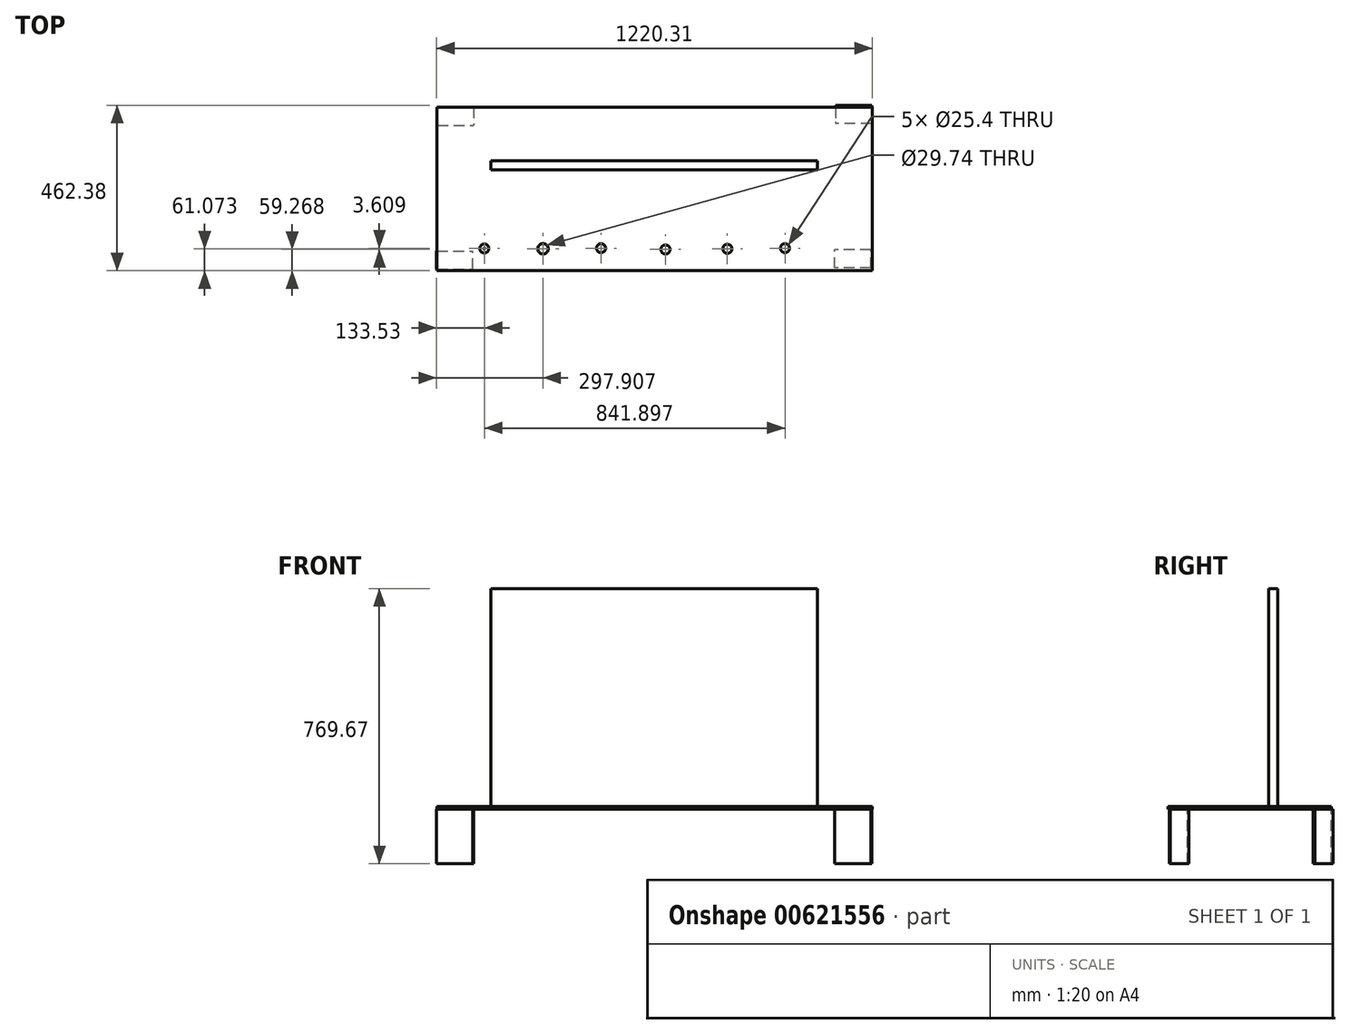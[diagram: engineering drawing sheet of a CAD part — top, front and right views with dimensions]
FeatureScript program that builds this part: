
annotation { "Feature Type Name" : "Feature", "Feature Type Description" : "" }
export const myFeature = defineFeature(function(context is Context, id is Id, definition is map)
    precondition{}
    {
        {
            var Q0;
            Q0=qCreatedBy(makeId("Front.planeOp"),FACE);
            var sketch = newSketch(context, id + "F0", { "sketchPlane" : qUnion([Q0])});
            skLineSegment(sketch, "E0.bottom", {"start": v(-46.83, 617.27) * mm, "end": v(867.57, 617.27) * mm});
            skLineSegment(sketch, "E0.top", {"start": v(-46.83, 7.67) * mm, "end": v(867.57, 7.67) * mm});
            skLineSegment(sketch, "E0.left", {"start": v(-46.83, 617.27) * mm, "end": v(-46.83, 7.67) * mm});
            skLineSegment(sketch, "E0.right", {"start": v(867.57, 617.27) * mm, "end": v(867.57, 7.67) * mm});
            skSolve(sketch);
        }
        {
            var Q0;
            Q0 = qSketchRegion(id + "F0", true);
            extrude(context, id + "F1", {"entities" : qUnion([Q0]), "depth" : 25.4 * mm, "offsetDistance" : 25.4 * mm});
        }
        {
            var Q0;
            Q0=qCreatedBy(makeId("Top.planeOp"),FACE);
            var sketch = newSketch(context, id + "F2", { "sketchPlane" : qUnion([Q0])});
            skLineSegment(sketch, "E1.bottom", {"start": v(-199.23, 152.4) * mm, "end": v(1019.97, 152.4) * mm});
            skLineSegment(sketch, "E1.top", {"start": v(-199.23, -304.8) * mm, "end": v(1019.97, -304.8) * mm});
            skLineSegment(sketch, "E1.left", {"start": v(-199.23, 152.4) * mm, "end": v(-199.23, -304.8) * mm});
            skLineSegment(sketch, "E1.right", {"start": v(1019.97, 152.4) * mm, "end": v(1019.97, -304.8) * mm});
            skSolve(sketch);
        }
        {
            var Q0;
            Q0 = qSketchRegion(id + "F2", true);
            var Q1;
            Q1=sQuery(id+"F2.wireOp",EDGE,"E1.top");
            var Q2;
            Q2=sQuery(id+"F2.wireOp",EDGE,"E1.left");
            var Q3;
            Q3=sQuery(id+"F2.wireOp",EDGE,"E1.right");
            extrude(context, id + "F3", {"entities" : qUnion([Q0]), "bodyType" : ToolBodyType.SURFACE, "surfaceEntities" : qUnion([Q1, Q2, Q3]), "oppositeDirection" : true, "depth" : 152.4 * mm, "offsetDistance" : 25.4 * mm});
        }
        {
            var Q0;
            Q0=qCreatedBy(makeId("Top.planeOp"),FACE);
            var sketch = newSketch(context, id + "F4", { "sketchPlane" : qUnion([Q0])});
            skLineSegment(sketch, "E2.bottom", {"start": v(-198.76, -303.45) * mm, "end": v(-97.16, -303.45) * mm});
            skLineSegment(sketch, "E2.top", {"start": v(-198.76, -252.65) * mm, "end": v(-97.16, -252.65) * mm});
            skLineSegment(sketch, "E2.left", {"start": v(-198.76, -303.45) * mm, "end": v(-198.76, -252.65) * mm});
            skLineSegment(sketch, "E2.right", {"start": v(-97.16, -303.45) * mm, "end": v(-97.16, -252.65) * mm});
            skLineSegment(sketch, "E3.bottom", {"start": v(1019.38, 154.87) * mm, "end": v(917.78, 154.87) * mm});
            skLineSegment(sketch, "E3.top", {"start": v(1019.38, 104.07) * mm, "end": v(917.78, 104.07) * mm});
            skLineSegment(sketch, "E3.left", {"start": v(1019.38, 154.87) * mm, "end": v(1019.38, 104.07) * mm});
            skLineSegment(sketch, "E3.right", {"start": v(917.78, 154.87) * mm, "end": v(917.78, 104.07) * mm});
            skLineSegment(sketch, "E4.bottom", {"start": v(1017.38, -300.09) * mm, "end": v(915.78, -300.09) * mm});
            skLineSegment(sketch, "E4.top", {"start": v(1017.38, -249.29) * mm, "end": v(915.78, -249.29) * mm});
            skLineSegment(sketch, "E4.left", {"start": v(1017.38, -300.09) * mm, "end": v(1017.38, -249.29) * mm});
            skLineSegment(sketch, "E4.right", {"start": v(915.78, -300.09) * mm, "end": v(915.78, -249.29) * mm});
            skLineSegment(sketch, "E5.bottom", {"start": v(-196.82, 149.6) * mm, "end": v(-95.22, 149.6) * mm});
            skLineSegment(sketch, "E5.top", {"start": v(-196.82, 98.8) * mm, "end": v(-95.22, 98.8) * mm});
            skLineSegment(sketch, "E5.left", {"start": v(-196.82, 149.6) * mm, "end": v(-196.82, 98.8) * mm});
            skLineSegment(sketch, "E5.right", {"start": v(-95.22, 149.6) * mm, "end": v(-95.22, 98.8) * mm});
            skSolve(sketch);
        }
        {
            var Q0;
            Q0 = qSketchRegion(id + "F4", true);
            extrude(context, id + "F5", {"entities" : qUnion([Q0]), "oppositeDirection" : true, "depth" : 152.4 * mm, "offsetDistance" : 25.4 * mm});
        }
        {
            var Q0;
            Q0=qCreatedBy(makeId("Top.planeOp"),FACE);
            var sketch = newSketch(context, id + "F6", { "sketchPlane" : qUnion([Q0])});
            skLineSegment(sketch, "E6.bottom", {"start": v(-197.65, 149.69) * mm, "end": v(1021.55, 149.69) * mm});
            skLineSegment(sketch, "E6.top", {"start": v(-197.65, -307.51) * mm, "end": v(1021.55, -307.51) * mm});
            skLineSegment(sketch, "E6.left", {"start": v(-197.65, 149.69) * mm, "end": v(-197.65, -307.51) * mm});
            skLineSegment(sketch, "E6.right", {"start": v(1021.55, 149.69) * mm, "end": v(1021.55, -307.51) * mm});
            skSolve(sketch);
        }
        {
            var Q0;
            Q0 = qSketchRegion(id + "F6", true);
            extrude(context, id + "F7", {"entities" : qUnion([Q0]), "depth" : 7.62 * mm, "offsetDistance" : 25.4 * mm});
        }
        {
            var Q0;
            Q0=qCreatedBy(makeId("Top.planeOp"),FACE);
            var sketch = newSketch(context, id + "F8", { "sketchPlane" : qUnion([Q0])});
            skCircle(sketch, "E7", {"center": v(-65.23, -245.47) * mm, "radius": 1.59 * mm});
            skCircle(sketch, "E8", {"center": v(-65.23, -245.47) * mm, "radius": 12.7 * mm});
            skCircle(sketch, "E9", {"center": v(99.15, -246.44) * mm, "radius": 14.87 * mm});
            skCircle(sketch, "E10", {"center": v(261.57, -244.63) * mm, "radius": 12.7 * mm});
            skCircle(sketch, "E11", {"center": v(442.04, -248.24) * mm, "radius": 12.7 * mm});
            skCircle(sketch, "E12", {"center": v(615.3, -246.44) * mm, "radius": 12.7 * mm});
            skCircle(sketch, "E13", {"center": v(776.67, -244.63) * mm, "radius": 12.7 * mm});
            skSolve(sketch);
        }
        {
            var Q0;
            Q0 = qSketchRegion(id + "F8", true);
            extrude(context, id + "F9", {"entities" : qUnion([Q0]), "operationType" : NewBodyOperationType.REMOVE, "endBound" : BoundingType.THROUGH_ALL, "depth" : 25.4 * mm, "offsetDistance" : 25.4 * mm});
        }
    });
